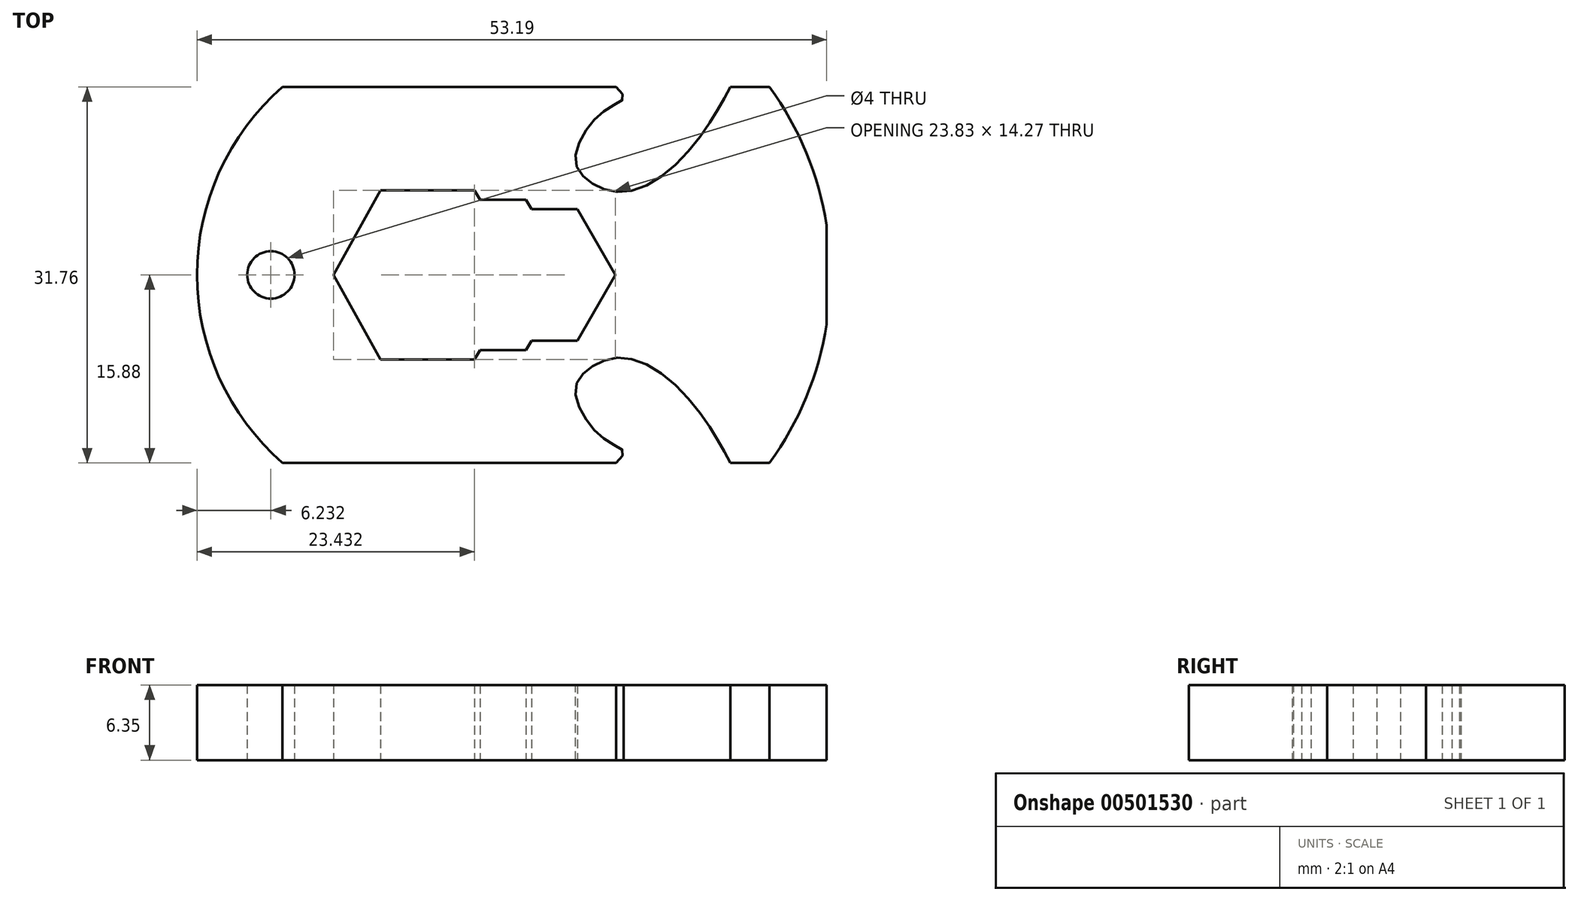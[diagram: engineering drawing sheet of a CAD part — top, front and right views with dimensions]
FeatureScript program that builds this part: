
annotation { "Feature Type Name" : "Feature", "Feature Type Description" : "" }
export const myFeature = defineFeature(function(context is Context, id is Id, definition is map)
    precondition{}
    {
        {
            var Q0;
            Q0=qCreatedBy(makeId("Top.planeOp"),FACE);
            var sketch = newSketch(context, id + "F0", { "sketchPlane" : qUnion([Q0])});
            skLineSegment(sketch, "E0.bottom", {"start": v(-25.4, 15.88) * mm, "end": v(25.4, 15.88) * mm});
            skLineSegment(sketch, "E0.top", {"start": v(-25.4, -15.87) * mm, "end": v(25.4, -15.87) * mm});
            skLineSegment(sketch, "E0.left", {"start": v(-25.4, 15.88) * mm, "end": v(-25.4, -15.87) * mm});
            skLineSegment(sketch, "E0.right", {"start": v(25.4, 15.87) * mm, "end": v(25.4, -15.87) * mm});
            skPoint(sketch, "E0.middle", {"position": v(0, 0) * mm});
            skLineSegment(sketch, "E1.MirrorCS", {"start": v(-76.2, 15.88) * mm, "end": v(-76.2, -15.87) * mm});
            skArc(sketch, "E2", {"start": v(-20.57, 15.87) * mm, "mid": v(-27.8, 0) * mm, "end": v(-20.57, -15.87) * mm});
            skArc(sketch, "E3", {"start": v(20.57, -15.87) * mm, "mid": v(25.72, 0) * mm, "end": v(20.57, 15.88) * mm});
            skCircle(sketch, "E4", {"center": v(-21.56, 0) * mm, "radius": 2 * mm});
            skLineSegment(sketch, "E5", {"start": v(-12.3, 7.14) * mm, "end": v(-16.27, 0) * mm});
            skLineSegment(sketch, "E6", {"start": v(-16.27, 0) * mm, "end": v(-12.3, -7.14) * mm});
            skLineSegment(sketch, "E7", {"start": v(-12.3, 7.14) * mm, "end": v(-4.35, 7.14) * mm});
            skLineSegment(sketch, "E8", {"start": v(-12.3, -7.14) * mm, "end": v(-4.35, -7.14) * mm});
            skLineSegment(sketch, "E9", {"start": v(-4.35, 7.14) * mm, "end": v(-3.9, 6.35) * mm});
            skLineSegment(sketch, "E10", {"start": v(-3.9, -6.35) * mm, "end": v(-4.35, -7.14) * mm});
            skLineSegment(sketch, "E11", {"start": v(-3.9, 6.35) * mm, "end": v(0, 6.35) * mm});
            skLineSegment(sketch, "E12", {"start": v(-3.9, -6.35) * mm, "end": v(0, -6.35) * mm});
            skLineSegment(sketch, "E13", {"start": v(0, 6.35) * mm, "end": v(0.46, 5.55) * mm});
            skLineSegment(sketch, "E14", {"start": v(0, -6.35) * mm, "end": v(0.46, -5.56) * mm});
            skLineSegment(sketch, "E15", {"start": v(0.46, 5.55) * mm, "end": v(4.35, 5.55) * mm});
            skLineSegment(sketch, "E16", {"start": v(0.46, -5.56) * mm, "end": v(4.34, -5.56) * mm});
            skLineSegment(sketch, "E17", {"start": v(4.35, 5.55) * mm, "end": v(7.56, 0) * mm});
            skLineSegment(sketch, "E18", {"start": v(4.34, -5.56) * mm, "end": v(7.56, 0) * mm});
            skArc(sketch, "E19", {"start": v(19.55, -15.88) * mm, "mid": v(24.54, 0) * mm, "end": v(19.55, 15.88) * mm});
            skFitSpline(sketch, "E20", {"points": [v(17.26, 15.87) * mm, v(15.73, 13.2) * mm, v(12.32, 9.02) * mm, v(8.3, 7) * mm, v(5.52, 7.77) * mm, v(4.2, 9.5) * mm, v(5.03, 12.15) * mm, v(6.97, 14.1) * mm, v(8.22, 14.93) * mm, v(7.6, 15.87) * mm], "startDerivative": vector(-11.4, -21.47) * mm, "endDerivative": vector(-14.56, 14.4) * mm});
            skFitSpline(sketch, "E21.MirrorCS", {"points": [v(17.26, -15.88) * mm, v(15.73, -13.2) * mm, v(12.32, -9.02) * mm, v(8.3, -7) * mm, v(5.52, -7.77) * mm, v(4.2, -9.5) * mm, v(5.03, -12.15) * mm, v(6.97, -14.1) * mm, v(8.22, -14.93) * mm, v(7.6, -15.88) * mm], "startDerivative": vector(-11.4, 21.47) * mm, "endDerivative": vector(-14.56, -14.4) * mm});
            skSolve(sketch);
        }
        {
            var Q0;
            {var subQ0=sQuery(id+"F0.wireOp",EDGE,"E2");var subQ1=sQuery(id+"F0.wireOp",EDGE,"E0.left");var subQ2=makeQuery(id+"F0.imprint","INTERSECT",VERTEX,{"disambiguationData":[OD(0.0)],"derivedFrom":[subQ1,subQ0]});Q0=makeQuery(id+"F0.imprint","IMPRINT",FACE,{"disambiguationData":[TD([[makeQuery(id+"F0.imprint","IMPRINT",EDGE,{"disambiguationData":[TD([[subQ2,-1.0]])],"derivedFrom":subQ1}),-1.0]])]});}
            var Q1;
            Q1=makeQuery(id+"F0.imprint","IMPRINT",FACE,{"disambiguationData":[TD([[makeQuery(id+"F0.imprint","IMPRINT",EDGE,{"derivedFrom":sQuery(id+"F0.wireOp",EDGE,"E4")}),-1.0]])]});
            var Q2;
            {var subQ0=sQuery(id+"F0.wireOp",EDGE,"E3");var subQ1=sQuery(id+"F0.wireOp",EDGE,"E0.right");var subQ2=makeQuery(id+"F0.imprint","INTERSECT",VERTEX,{"disambiguationData":[OD(0.0)],"derivedFrom":[subQ1,subQ0]});Q2=makeQuery(id+"F0.imprint","IMPRINT",FACE,{"disambiguationData":[TD([[makeQuery(id+"F0.imprint","IMPRINT",EDGE,{"disambiguationData":[TD([[subQ2,-1.0]])],"derivedFrom":subQ1}),1.0]])]});}
            var Q3;
            {var subQ5=sQuery(id+"F0.wireOp",EDGE,"E19");Q3=makeQuery(id+"F0.imprint","IMPRINT",FACE,{"disambiguationData":[TD([[makeQuery(id+"F0.imprint","IMPRINT",EDGE,{"derivedFrom":subQ5}),-1.0]])]});}
            extrude(context, id + "F1", {"entities" : qUnion([Q0, Q1, Q2, Q3]), "depth" : 6.35 * mm});
        }
    });
